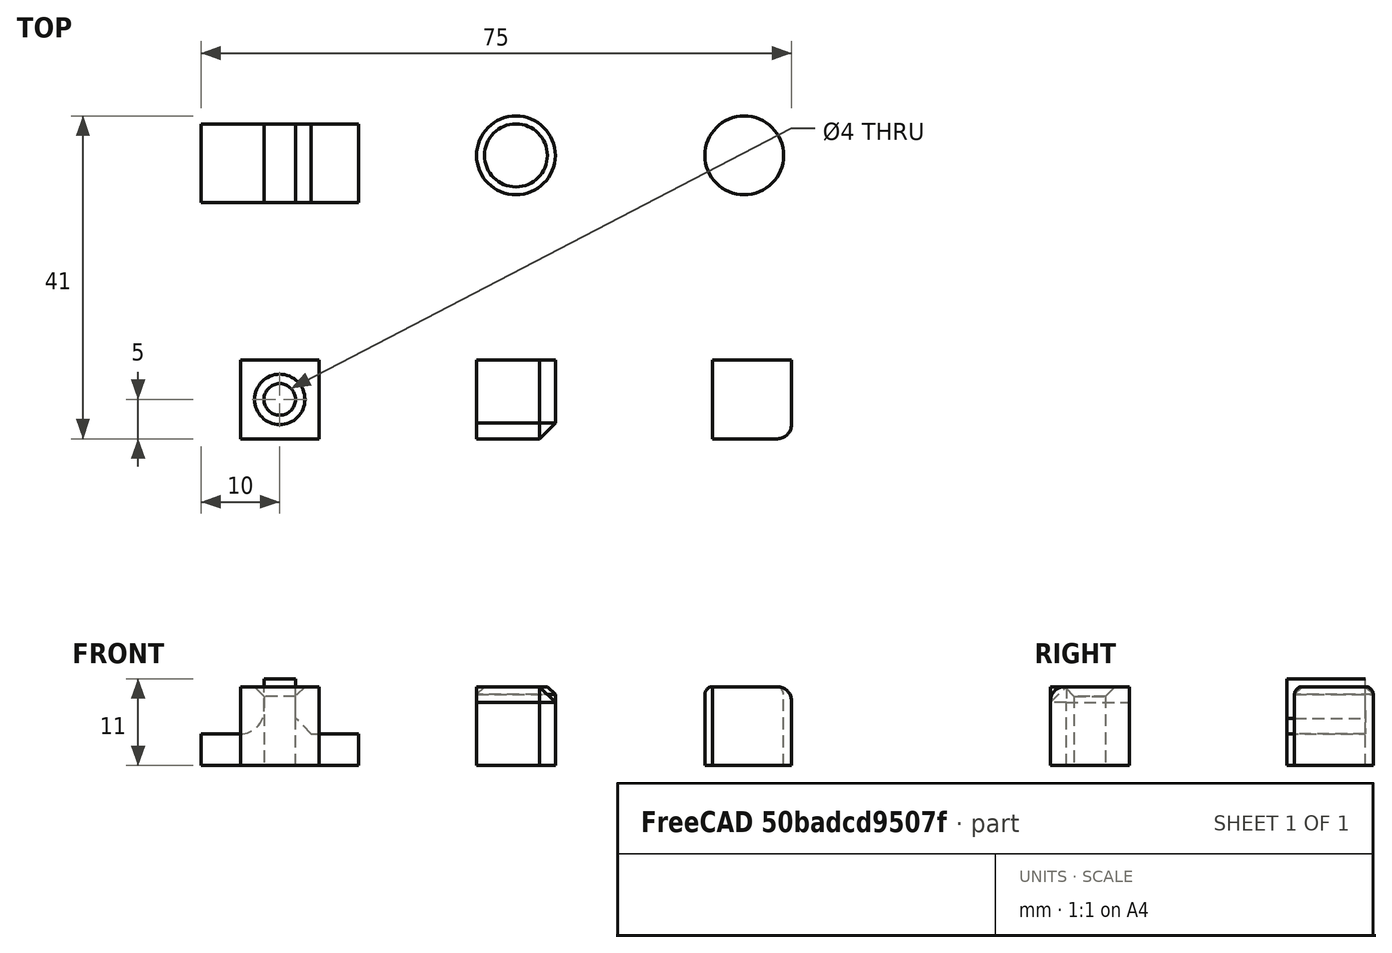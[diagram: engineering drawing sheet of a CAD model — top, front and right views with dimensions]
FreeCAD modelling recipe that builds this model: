
FCSTD DOCUMENT  (FreeCAD 1.0R39285 (Git))
Label: ojt1_t12p01_roundings_chamfers_reinforcements
License: All rights reserved
objects: Part::Box×6, Part::Chamfer×4, Part::Cylinder×3, Part::Cut×3, Part::Fillet×3
note: 19 computed .brp shape members not serialized (recipe doc carries the construction recipe); baked Part::Feature solids carry a one-line shape summary decoded from their .brp

FEATURE [Part::Box] Box  label="Cub"
  AttacherType = Attacher::AttachEngine3D
  Height = 10
  Length = 10
  Width = 10
FEATURE [Part::Box] Box001  label="Cub001"
  AttacherType = Attacher::AttachEngine3D
  Height = 10
  Length = 10
  Placement = pos=(30,0,0) rot=(0,0,1;0rad)
  Width = 10
FEATURE [Part::Box] Box002  label="Cub002"
  AttacherType = Attacher::AttachEngine3D
  Height = 10
  Length = 10
  Placement = pos=(60,0,0) rot=(0,0,1;0rad)
  Width = 10
FEATURE [Part::Cylinder] Cylinder  label="Cilindre"
  Angle = 360
  AttacherType = Attacher::AttachEngine3D
  FirstAngle = 0
  Height = 12
  Placement = pos=(5,5,-1) rot=(0,0,1;0rad)
  Radius = 2
  SecondAngle = 0
FEATURE [Part::Cylinder] Cylinder001  label="Cilindre001"
  Angle = 360
  AttacherType = Attacher::AttachEngine3D
  FirstAngle = 0
  Height = 10
  Placement = pos=(35,36,0) rot=(0,0,1;0rad)
  Radius = 5
  SecondAngle = 0
FEATURE [Part::Box] Box003  label="Cub003"
  AttacherType = Attacher::AttachEngine3D
  Height = 11
  Length = 20
  Placement = pos=(-5,30,0) rot=(0,0,1;0rad)
  Width = 10
FEATURE [Part::Box] Box004  label="Cub004"
  AttacherType = Attacher::AttachEngine3D
  Height = 10
  Length = 10
  Placement = pos=(-7,30,4) rot=(0,0,1;0rad)
  Width = 10
FEATURE [Part::Box] Box005  label="Cub005"
  AttacherType = Attacher::AttachEngine3D
  Height = 10
  Length = 10
  Placement = pos=(7,30,4) rot=(0,0,1;0rad)
  Width = 10
FEATURE [Part::Cut] Cut
  Base = -> Box
  Refine = true
  Tool = -> Cylinder
FEATURE [Part::Cylinder] Cylinder002  label="Cilindre002"
  Angle = 360
  AttacherType = Attacher::AttachEngine3D
  FirstAngle = 0
  Height = 10
  Placement = pos=(64,36,0) rot=(0,0,1;0rad)
  Radius = 5
  SecondAngle = 0
FEATURE [Part::Cut] Cut001
  Base = -> Box003
  Refine = true
  Tool = -> Box004
FEATURE [Part::Cut] Cut002
  Base = -> Cut001
  Refine = true
  Tool = -> Box005
FEATURE [Part::Fillet] Fillet
  Base = -> Box002
  EdgeLinks = -> Box002 [Edge5,Edge6,Edge10]
  Edges = 3 edges r=1.8: [Edge5,Edge6,Edge10]
FEATURE [Part::Chamfer] Chamfer
  Base = -> Box001
  EdgeLinks = -> Box001 [Edge5,Edge6,Edge10]
  Edges = 3 edges r=2: [Edge5,Edge6,Edge10]
FEATURE [Part::Chamfer] Chamfer001
  Base = -> Cut
  EdgeLinks = -> Cut [Edge10]
  Edges = 1 edges r=1.2: [Edge10]
FEATURE [Part::Fillet] Fillet001
  Base = -> Cylinder002
  EdgeLinks = -> Cylinder002 [Edge3]
  Edges = 1 edges r=1: [Edge3]
FEATURE [Part::Chamfer] Chamfer002
  Base = -> Cylinder001
  EdgeLinks = -> Cylinder001 [Edge3]
  Edges = 1 edges r=1: [Edge3]
FEATURE [Part::Chamfer] Chamfer003
  Base = -> Cut002
  EdgeLinks = -> Cut002 [Edge22]
  Edges = 1 edges r=2: [Edge22]
FEATURE [Part::Fillet] Fillet002
  Base = -> Chamfer003
  EdgeLinks = -> Chamfer003 [Edge26]
  Edges = 1 edges r=3: [Edge26]
